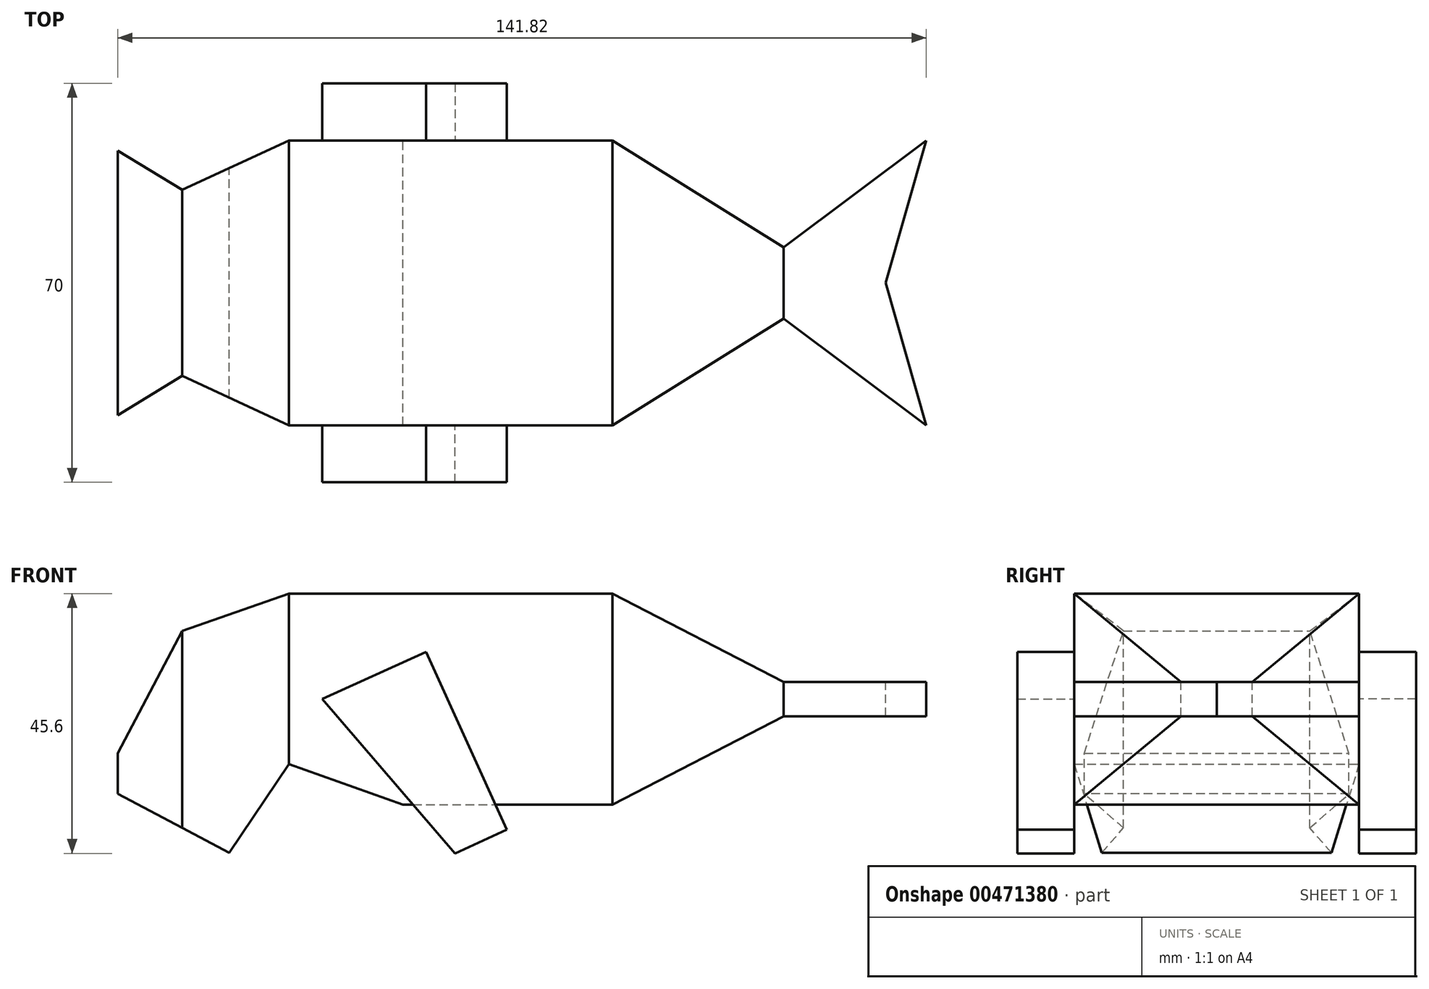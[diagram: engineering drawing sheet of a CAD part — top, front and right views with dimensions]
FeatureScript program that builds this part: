
annotation { "Feature Type Name" : "Feature", "Feature Type Description" : "" }
export const myFeature = defineFeature(function(context is Context, id is Id, definition is map)
    precondition{}
    {
        {
            var Q0;
            Q0=qCreatedBy(makeId("Front.planeOp"),FACE);
            var sketch = newSketch(context, id + "F0", { "sketchPlane" : qUnion([Q0])});
            skLineSegment(sketch, "E0.bottom", {"start": v(-18.4, 18.54) * mm, "end": v(18.4, 18.54) * mm});
            skLineSegment(sketch, "E0.top", {"start": v(-18.4, -18.54) * mm, "end": v(18.4, -18.54) * mm});
            skPoint(sketch, "E0.middle", {"position": v(0, 0) * mm});
            skLineSegment(sketch, "E1", {"start": v(-18.4, -18.54) * mm, "end": v(-38.4, -11.42) * mm});
            skLineSegment(sketch, "E2", {"start": v(-18.4, 18.54) * mm, "end": v(-38.4, 18.54) * mm});
            skPoint(sketch, "E3.endSnap0", {"position": v(18.4, 0) * mm});
            skLineSegment(sketch, "E4", {"start": v(48.4, 3) * mm, "end": v(18.4, 18.54) * mm});
            skLineSegment(sketch, "E5", {"start": v(48.4, -3) * mm, "end": v(18.4, -18.54) * mm});
            skLineSegment(sketch, "E6", {"start": v(48.4, 3) * mm, "end": v(73.4, 3) * mm});
            skLineSegment(sketch, "E7", {"start": v(48.4, -3) * mm, "end": v(73.4, -3) * mm});
            skLineSegment(sketch, "E8", {"start": v(73.4, -3) * mm, "end": v(73.4, 3) * mm});
            skLineSegment(sketch, "E9", {"start": v(-38.4, 18.54) * mm, "end": v(-57.1, 11.98) * mm});
            skLineSegment(sketch, "E10", {"start": v(-57.1, 11.98) * mm, "end": v(-71.37, -15.09) * mm});
            skLineSegment(sketch, "E11", {"start": v(-71.37, -15.09) * mm, "end": v(-48.88, -26.93) * mm});
            skLineSegment(sketch, "E12", {"start": v(-48.88, -26.93) * mm, "end": v(-38.4, -11.42) * mm});
            skSolve(sketch);
        }
        {
            var Q0;
            Q0 = qSketchRegion(id + "F0", true);
            extrude(context, id + "F1", {"entities" : qUnion([Q0]), "endBound" : BoundingType.SYMMETRIC, "depth" : 50 * mm});
        }
        {
            var Q0;
            Q0=makeQuery(id+"F1.opExtrude","SWEPT_FACE",FACE,{"disambiguationData":[OSD([sQuery(id+"F0.wireOp",EDGE,"E0.bottom"),sQuery(id+"F0.wireOp",EDGE,"E2")])]});
            var sketch = newSketch(context, id + "F2", { "sketchPlane" : qUnion([Q0])});
            skLineSegment(sketch, "E13.0", {"start": v(-71.37, -25) * mm, "end": v(-71.37, 25) * mm});
            skLineSegment(sketch, "E14", {"start": v(-38.4, -25) * mm, "end": v(-57.1, -16.34) * mm});
            skLineSegment(sketch, "E15", {"start": v(-57.1, -16.34) * mm, "end": v(-71.37, -25) * mm});
            skLineSegment(sketch, "E16", {"start": v(-38.4, -25) * mm, "end": v(18.4, -25) * mm});
            skLineSegment(sketch, "E17", {"start": v(18.4, -25) * mm, "end": v(48.4, -6.27) * mm});
            skLineSegment(sketch, "E18.MirrorCS", {"start": v(-57.1, 16.34) * mm, "end": v(-71.37, 25) * mm});
            skLineSegment(sketch, "E19.MirrorCS", {"start": v(-38.4, 25) * mm, "end": v(-57.1, 16.34) * mm});
            skLineSegment(sketch, "E20.MirrorCS", {"start": v(-38.4, 25) * mm, "end": v(18.4, 25) * mm});
            skLineSegment(sketch, "E21.MirrorCS", {"start": v(18.4, 25) * mm, "end": v(48.4, 6.27) * mm});
            skLineSegment(sketch, "E22.bottom", {"start": v(-94.32, 45) * mm, "end": v(126.06, 45) * mm});
            skLineSegment(sketch, "E22.top", {"start": v(-94.32, -58.43) * mm, "end": v(126.06, -58.43) * mm});
            skLineSegment(sketch, "E22.left", {"start": v(-94.32, 45) * mm, "end": v(-94.32, -58.43) * mm});
            skLineSegment(sketch, "E22.right", {"start": v(126.06, 45) * mm, "end": v(126.06, -58.43) * mm});
            skPoint(sketch, "E23.0", {"position": v(73.4, -25) * mm});
            skPoint(sketch, "E24.0", {"position": v(73.4, 25) * mm});
            skLineSegment(sketch, "E25", {"start": v(48.4, -6.27) * mm, "end": v(73.4, -25) * mm});
            skLineSegment(sketch, "E26", {"start": v(73.4, -25) * mm, "end": v(66.33, 0) * mm});
            skLineSegment(sketch, "E27", {"start": v(66.33, 0) * mm, "end": v(73.4, 25) * mm});
            skLineSegment(sketch, "E28", {"start": v(73.4, 25) * mm, "end": v(48.4, 6.27) * mm});
            skSolve(sketch);
        }
        {
            var Q0;
            Q0 = qSketchRegion(id + "F2", true);
            extrude(context, id + "F3", {"entities" : qUnion([Q0]), "operationType" : NewBodyOperationType.REMOVE, "oppositeDirection" : true, "depth" : 49.4 * mm});
        }
        {
            var Q0;
            Q0=makeQuery(id+"F1.opExtrude","SWEPT_FACE",FACE,{"disambiguationData":[OSD([sQuery(id+"F0.wireOp",EDGE,"E10")])]});
            var sketch = newSketch(context, id + "F4", { "sketchPlane" : qUnion([Q0])});
            skArc(sketch, "E29", {"start": v(-5.88, -25.8) * mm, "mid": v(-9.74, -20.64) * mm, "end": v(-14.46, -25.04) * mm});
            skArc(sketch, "E30", {"start": v(-14.38, -33.95) * mm, "mid": v(-10.13, -38.2) * mm, "end": v(-5.88, -33.95) * mm});
            skLineSegment(sketch, "E31", {"start": v(-5.88, -33.95) * mm, "end": v(-5.88, -24.95) * mm});
            skLineSegment(sketch, "E32", {"start": v(-14.46, -24.95) * mm, "end": v(-14.38, -33.95) * mm});
            skCircle(sketch, "E33", {"center": v(-10.13, -33.95) * mm, "radius": 3.46 * mm});
            skLineSegment(sketch, "E34.MirrorCS", {"start": v(5.88, -33.95) * mm, "end": v(5.88, -24.95) * mm});
            skCircle(sketch, "E35.MirrorC", {"center": v(10.13, -33.95) * mm, "radius": 3.46 * mm});
            skArc(sketch, "E36.MirrorCS", {"start": v(14.38, -33.95) * mm, "mid": v(10.13, -38.2) * mm, "end": v(5.88, -33.95) * mm});
            skLineSegment(sketch, "E37.MirrorCS", {"start": v(14.46, -24.95) * mm, "end": v(14.38, -33.95) * mm});
            skArc(sketch, "E38.MirrorCS", {"start": v(5.88, -25.8) * mm, "mid": v(9.74, -20.64) * mm, "end": v(14.46, -25.04) * mm});
            skSolve(sketch);
        }
        {
            var Q0;
            Q0=makeQuery(id+"F1.opExtrude","CAP_FACE",FACE,{"disambiguationData":[OSD([sQuery(id+"F0.wireOp",EDGE,"E0.bottom"),sQuery(id+"F0.wireOp",EDGE,"E0.top"),sQuery(id+"F0.wireOp",EDGE,"E1"),sQuery(id+"F0.wireOp",EDGE,"E2"),sQuery(id+"F0.wireOp",EDGE,"E4"),sQuery(id+"F0.wireOp",EDGE,"E5"),sQuery(id+"F0.wireOp",EDGE,"E6"),sQuery(id+"F0.wireOp",EDGE,"E7"),sQuery(id+"F0.wireOp",EDGE,"E8"),sQuery(id+"F0.wireOp",EDGE,"E9"),sQuery(id+"F0.wireOp",EDGE,"E10"),sQuery(id+"F0.wireOp",EDGE,"E11"),sQuery(id+"F0.wireOp",EDGE,"E12")])],"isStart":false});
            var sketch = newSketch(context, id + "F5", { "sketchPlane" : qUnion([Q0])});
            skLineSegment(sketch, "E39", {"start": v(-32.56, 0) * mm, "end": v(-18.4, -31.2) * mm});
            skLineSegment(sketch, "E40.0", {"start": v(-14.34, 8.27) * mm, "end": v(-0.18, -22.92) * mm});
            skLineSegment(sketch, "E41", {"start": v(-32.56, 0) * mm, "end": v(-14.34, 8.27) * mm});
            skLineSegment(sketch, "E42", {"start": v(-18.4, -31.2) * mm, "end": v(-0.18, -22.92) * mm});
            skSolve(sketch);
        }
        {
            var Q0;
            Q0 = qSketchRegion(id + "F5", true);
            extrude(context, id + "F6", {"entities" : qUnion([Q0]), "operationType" : NewBodyOperationType.ADD, "depth" : 10 * mm});
        }
        {
            var Q0;
            Q0=makeQuery(id+"F1.opExtrude","CAP_FACE",FACE,{"disambiguationData":[OSD([sQuery(id+"F0.wireOp",EDGE,"E0.bottom"),sQuery(id+"F0.wireOp",EDGE,"E0.top"),sQuery(id+"F0.wireOp",EDGE,"E1"),sQuery(id+"F0.wireOp",EDGE,"E2"),sQuery(id+"F0.wireOp",EDGE,"E4"),sQuery(id+"F0.wireOp",EDGE,"E5"),sQuery(id+"F0.wireOp",EDGE,"E6"),sQuery(id+"F0.wireOp",EDGE,"E7"),sQuery(id+"F0.wireOp",EDGE,"E8"),sQuery(id+"F0.wireOp",EDGE,"E9"),sQuery(id+"F0.wireOp",EDGE,"E10"),sQuery(id+"F0.wireOp",EDGE,"E11"),sQuery(id+"F0.wireOp",EDGE,"E12")])],"isStart":false});
            var sketch = newSketch(context, id + "F7", { "sketchPlane" : qUnion([Q0])});
            skLineSegment(sketch, "E43.0", {"start": v(-14.34, 8.27) * mm, "end": v(-0.18, -22.92) * mm});
            skPoint(sketch, "E44.1", {"position": v(-25.47, -15.6) * mm});
            skLineSegment(sketch, "E45", {"start": v(-32.56, 0) * mm, "end": v(-9.29, -27.06) * mm});
            skLineSegment(sketch, "E46", {"start": v(-32.56, 0) * mm, "end": v(-27.68, -47.24) * mm});
            skLineSegment(sketch, "E47", {"start": v(-27.68, -47.24) * mm, "end": v(-7.97, -40.13) * mm});
            skLineSegment(sketch, "E48", {"start": v(-7.97, -40.13) * mm, "end": v(-9.29, -27.06) * mm});
            skSolve(sketch);
        }
        {
            var Q0;
            Q0 = qSketchRegion(id + "F7", true);
            extrude(context, id + "F8", {"entities" : qUnion([Q0]), "operationType" : NewBodyOperationType.REMOVE, "depth" : 25 * mm});
        }
        {
            var Q0;
            Q0=makeQuery(id+"F1.opExtrude","CAP_FACE",FACE,{"disambiguationData":[OSD([sQuery(id+"F0.wireOp",EDGE,"E0.bottom"),sQuery(id+"F0.wireOp",EDGE,"E0.top"),sQuery(id+"F0.wireOp",EDGE,"E1"),sQuery(id+"F0.wireOp",EDGE,"E2"),sQuery(id+"F0.wireOp",EDGE,"E4"),sQuery(id+"F0.wireOp",EDGE,"E5"),sQuery(id+"F0.wireOp",EDGE,"E6"),sQuery(id+"F0.wireOp",EDGE,"E7"),sQuery(id+"F0.wireOp",EDGE,"E8"),sQuery(id+"F0.wireOp",EDGE,"E9"),sQuery(id+"F0.wireOp",EDGE,"E10"),sQuery(id+"F0.wireOp",EDGE,"E11"),sQuery(id+"F0.wireOp",EDGE,"E12")])],"isStart":true});
            var sketch = newSketch(context, id + "F9", { "sketchPlane" : qUnion([Q0])});
            skLineSegment(sketch, "E49.0.0", {"start": v(32.56, 0) * mm, "end": v(9.29, -27.06) * mm});
            skLineSegment(sketch, "E49.0.1", {"start": v(9.29, -27.06) * mm, "end": v(0.18, -22.92) * mm});
            skLineSegment(sketch, "E49.0.2", {"start": v(0.18, -22.92) * mm, "end": v(14.34, 8.27) * mm});
            skLineSegment(sketch, "E49.0.3", {"start": v(14.34, 8.27) * mm, "end": v(32.56, 0) * mm});
            skSolve(sketch);
        }
        {
            var Q0;
            Q0 = qSketchRegion(id + "F9", true);
            extrude(context, id + "F10", {"entities" : qUnion([Q0]), "operationType" : NewBodyOperationType.ADD, "depth" : 10 * mm});
        }
        {
            var Q0;
            Q0=makeQuery(id+"F1.opExtrude","SWEPT_FACE",FACE,{"disambiguationData":[OSD([sQuery(id+"F0.wireOp",EDGE,"E11")])]});
            var sketch = newSketch(context, id + "F11", { "sketchPlane" : qUnion([Q0])});
            skArc(sketch, "E50", {"start": v(-45.5, -14.51) * mm, "mid": v(-36.1, 0) * mm, "end": v(-45.5, 14.51) * mm});
            skArc(sketch, "E51", {"start": v(-45.5, -14.51) * mm, "mid": v(-40.92, 0) * mm, "end": v(-45.5, 14.51) * mm});
            skSolve(sketch);
        }
        {
            var Q0;
            Q0=qCreatedBy(makeId("Front.planeOp"),FACE);
            var sketch = newSketch(context, id + "F12", { "sketchPlane" : qUnion([Q0])});
            skLineSegment(sketch, "E52", {"start": v(-68.43, -4.6) * mm, "end": v(-68.43, -23.5) * mm});
            skLineSegment(sketch, "E53", {"start": v(-68.43, -23.5) * mm, "end": v(-78.39, -19.23) * mm});
            skLineSegment(sketch, "E54", {"start": v(-78.39, -19.23) * mm, "end": v(-68.43, -4.6) * mm});
            skSolve(sketch);
        }
        {
            var Q0;
            Q0 = qSketchRegion(id + "F12", true);
            extrude(context, id + "F13", {"entities" : qUnion([Q0]), "operationType" : NewBodyOperationType.REMOVE, "endBound" : BoundingType.SYMMETRIC, "oppositeDirection" : true, "depth" : 62.6 * mm});
        }
    });
